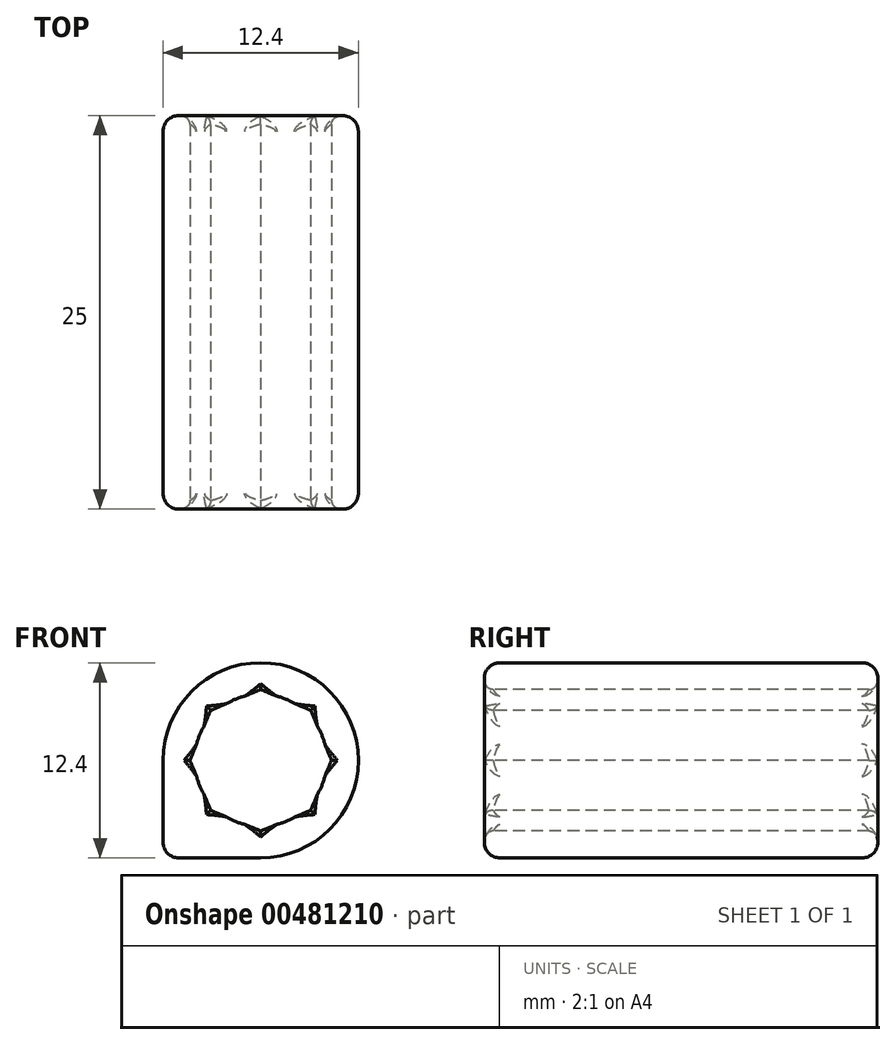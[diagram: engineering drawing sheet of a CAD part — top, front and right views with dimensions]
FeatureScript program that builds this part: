
annotation { "Feature Type Name" : "Feature", "Feature Type Description" : "" }
export const myFeature = defineFeature(function(context is Context, id is Id, definition is map)
    precondition{}
    {
        {
            var Q0;
            Q0=qCreatedBy(makeId("Front.planeOp"),FACE);
            var sketch = newSketch(context, id + "F0", { "sketchPlane" : qUnion([Q0])});
            skCircle(sketch, "E0", {"center": v(6.2, 6.2) * mm, "radius": 4.2 * mm});
            skCircle(sketch, "E1", {"center": v(6.2, 6.2) * mm, "radius": 6.2 * mm});
            skLineSegment(sketch, "E2", {"start": v(0, 0) * mm, "end": v(0, 6.2) * mm});
            skLineSegment(sketch, "E3", {"start": v(0, 0) * mm, "end": v(6.2, 0) * mm});
            skSolve(sketch);
        }
        {
            var Q0;
            Q0=makeQuery(id+"F0.imprint","IMPRINT",FACE,{"disambiguationData":[TD([[makeQuery(id+"F0.imprint","IMPRINT",EDGE,{"derivedFrom":sQuery(id+"F0.wireOp",EDGE,"E0")}),-1.0]])]});
            var Q1;
            {var subQ0=sQuery(id+"F0.wireOp",EDGE,"E2");Q1=makeQuery(id+"F0.imprint","IMPRINT",FACE,{"disambiguationData":[TD([[makeQuery(id+"F0.imprint","IMPRINT",EDGE,{"derivedFrom":subQ0}),-1.0]])]});}
            extrude(context, id + "F1", {"entities" : qUnion([Q0, Q1]), "oppositeDirection" : true, "depth" : 25 * mm});
        }
        {
            var Q0;
            Q0=makeQuery(id+"F1.opExtrude","CAP_FACE",FACE,{"disambiguationData":[OSD([sQuery(id+"F0.wireOp",EDGE,"E0"),sQuery(id+"F0.wireOp",EDGE,"E1"),sQuery(id+"F0.wireOp",EDGE,"E2"),sQuery(id+"F0.wireOp",EDGE,"E3")])],"isStart":false});
            var Q1;
            Q1=makeQuery(id+"F1.opExtrude","CAP_FACE",FACE,{"disambiguationData":[OSD([sQuery(id+"F0.wireOp",EDGE,"E0"),sQuery(id+"F0.wireOp",EDGE,"E1"),sQuery(id+"F0.wireOp",EDGE,"E2"),sQuery(id+"F0.wireOp",EDGE,"E3")])],"isStart":true});
            var Q2;
            Q2=makeQuery(id+"F1.opExtrude","SWEPT_EDGE",EDGE,{"disambiguationData":[OSD([sQuery(id+"F0.wireOp",EDGE,"E2"),sQuery(id+"F0.wireOp",EDGE,"E3")])]});
            fillet(context, id + "F2", {"entities" : qUnion([Q0, Q1, Q2]), "radius" : 1 * mm, "tangentPropagation" : true, "allowEdgeOverflow" : false});
        }
        {
            var Q0;
            Q0=qCreatedBy(makeId("Front.planeOp"),FACE);
            var sketch = newSketch(context, id + "F3", { "sketchPlane" : qUnion([Q0])});
            skCircle(sketch, "E4.cCircle", {"center": v(6.2, 6.2) * mm, "radius": 4.15 * mm, "construction": true});
            skLineSegment(sketch, "E4.0", {"start": v(9.38, 3.02) * mm, "end": v(6.2, 1.7) * mm});
            skLineSegment(sketch, "E4.1", {"start": v(6.2, 1.7) * mm, "end": v(3.02, 3.02) * mm});
            skLineSegment(sketch, "E4.2", {"start": v(3.02, 3.02) * mm, "end": v(1.7, 6.2) * mm});
            skLineSegment(sketch, "E4.3", {"start": v(1.7, 6.2) * mm, "end": v(3.02, 9.38) * mm});
            skLineSegment(sketch, "E4.4", {"start": v(3.02, 9.38) * mm, "end": v(6.2, 10.7) * mm});
            skLineSegment(sketch, "E4.5", {"start": v(6.2, 10.7) * mm, "end": v(9.38, 9.38) * mm});
            skLineSegment(sketch, "E4.6", {"start": v(9.38, 9.38) * mm, "end": v(10.7, 6.2) * mm});
            skLineSegment(sketch, "E4.7", {"start": v(10.7, 6.2) * mm, "end": v(9.38, 3.02) * mm});
            skPoint(sketch, "E4.0.midPoint", {"position": v(7.79, 2.37) * mm});
            skLineSegment(sketch, "E5", {"start": v(6.2, 0) * mm, "end": v(6.2, 12.4) * mm, "construction": true});
            skSolve(sketch);
        }
        {
            var Q0;
            Q0 = qSketchRegion(id + "F3", true);
            extrude(context, id + "F4", {"entities" : qUnion([Q0]), "operationType" : NewBodyOperationType.REMOVE, "endBound" : BoundingType.THROUGH_ALL, "oppositeDirection" : true, "depth" : 25 * mm});
        }
        {
            var Q0;
            Q0=makeQuery(id+"F4.boolean.opBoolean","SPLIT",FACE,{"disambiguationData":[TD([makeQuery(id+"F4.opExtrude","SWEPT_FACE",FACE,{"disambiguationData":[OSD([sQuery(id+"F3.wireOp",EDGE,"E4.0")])]})])],"derivedFrom":makeQuery(id+"F1.opExtrude","SWEPT_FACE",FACE,{"disambiguationData":[OSD([sQuery(id+"F0.wireOp",EDGE,"E0")])]})});
            var Q1;
            Q1=makeQuery(id+"F4.boolean.opBoolean","SPLIT",FACE,{"disambiguationData":[TD([makeQuery(id+"F4.opExtrude","SWEPT_FACE",FACE,{"disambiguationData":[OSD([sQuery(id+"F3.wireOp",EDGE,"E4.7")])]})])],"derivedFrom":makeQuery(id+"F1.opExtrude","SWEPT_FACE",FACE,{"disambiguationData":[OSD([sQuery(id+"F0.wireOp",EDGE,"E0")])]})});
            var Q2;
            Q2=makeQuery(id+"F4.boolean.opBoolean","SPLIT",FACE,{"disambiguationData":[TD([makeQuery(id+"F4.opExtrude","SWEPT_FACE",FACE,{"disambiguationData":[OSD([sQuery(id+"F3.wireOp",EDGE,"E4.6")])]})])],"derivedFrom":makeQuery(id+"F1.opExtrude","SWEPT_FACE",FACE,{"disambiguationData":[OSD([sQuery(id+"F0.wireOp",EDGE,"E0")])]})});
            var Q3;
            Q3=makeQuery(id+"F4.boolean.opBoolean","SPLIT",FACE,{"disambiguationData":[TD([makeQuery(id+"F4.opExtrude","SWEPT_FACE",FACE,{"disambiguationData":[OSD([sQuery(id+"F3.wireOp",EDGE,"E4.5")])]})])],"derivedFrom":makeQuery(id+"F1.opExtrude","SWEPT_FACE",FACE,{"disambiguationData":[OSD([sQuery(id+"F0.wireOp",EDGE,"E0")])]})});
            var Q4;
            Q4=makeQuery(id+"F4.boolean.opBoolean","SPLIT",FACE,{"disambiguationData":[TD([makeQuery(id+"F4.opExtrude","SWEPT_FACE",FACE,{"disambiguationData":[OSD([sQuery(id+"F3.wireOp",EDGE,"E4.4")])]})])],"derivedFrom":makeQuery(id+"F1.opExtrude","SWEPT_FACE",FACE,{"disambiguationData":[OSD([sQuery(id+"F0.wireOp",EDGE,"E0")])]})});
            var Q5;
            Q5=makeQuery(id+"F4.boolean.opBoolean","SPLIT",FACE,{"disambiguationData":[TD([makeQuery(id+"F4.opExtrude","SWEPT_FACE",FACE,{"disambiguationData":[OSD([sQuery(id+"F3.wireOp",EDGE,"E4.3")])]})])],"derivedFrom":makeQuery(id+"F1.opExtrude","SWEPT_FACE",FACE,{"disambiguationData":[OSD([sQuery(id+"F0.wireOp",EDGE,"E0")])]})});
            var Q6;
            Q6=makeQuery(id+"F4.boolean.opBoolean","SPLIT",FACE,{"disambiguationData":[TD([makeQuery(id+"F4.opExtrude","SWEPT_FACE",FACE,{"disambiguationData":[OSD([sQuery(id+"F3.wireOp",EDGE,"E4.2")])]})])],"derivedFrom":makeQuery(id+"F1.opExtrude","SWEPT_FACE",FACE,{"disambiguationData":[OSD([sQuery(id+"F0.wireOp",EDGE,"E0")])]})});
            var Q7;
            Q7=makeQuery(id+"F4.boolean.opBoolean","SPLIT",FACE,{"disambiguationData":[TD([makeQuery(id+"F4.opExtrude","SWEPT_FACE",FACE,{"disambiguationData":[OSD([sQuery(id+"F3.wireOp",EDGE,"E4.1")])]})])],"derivedFrom":makeQuery(id+"F1.opExtrude","SWEPT_FACE",FACE,{"disambiguationData":[OSD([sQuery(id+"F0.wireOp",EDGE,"E0")])]})});
            fillet(context, id + "F5", {"entities" : qUnion([Q0, Q1, Q2, Q3, Q4, Q5, Q6, Q7]), "radius" : .5 * mm, "tangentPropagation" : true, "allowEdgeOverflow" : false});
        }
    });
